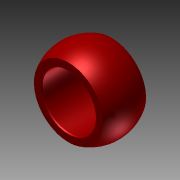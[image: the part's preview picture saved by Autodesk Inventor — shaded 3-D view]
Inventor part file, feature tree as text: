
AUTODESK INVENTOR PART (.ipt)
format: ipt  version: 2011 (Build 150239000, 239)  size: 107,008 bytes
history: native  units: mm (DEFAULTED — no unit token found)
features: sketch x2, revolve x1, extrude x1, hole x1, chamfer x1
ambient origin geometry x8: Origin, YZ Plane, XZ Plane, XY Plane, X Axis, Y Axis, Z Axis, Center Point
bodies: Solid1 (feature_tree)
feature tree (6):
  revolve  "Revolution1"  Angle=90.0deg
  extrude  "Extrusion3"  Depth=25.4mm TaperAngle=0.0deg
  hole  "Hole1"  [1 undecoded]
  chamfer  "Chamfer1"  Distance=0.3048mm Angle=30.0deg
  sketch  "Sketch1"  dims[d0=24.003mm d1=90.0deg]
  sketch  "Sketch4"  dims[d8=12.7mm d9=25.4mm d10=0.0mm d11=25.4mm d12=25.4mm d13=15.875mm d14=12.7mm d15=9.525mm d16=6.35mm d17=14.3117mm d18=19.05mm d19=20.594885mm d20=0.3048mm d21=3.175mm d22=30.0deg]
note: 1 required parameter value undecoded (feature->parameter linkage not recoverable at this tier; creation-order binding heuristic only, values carry confidence <= 0.55)
